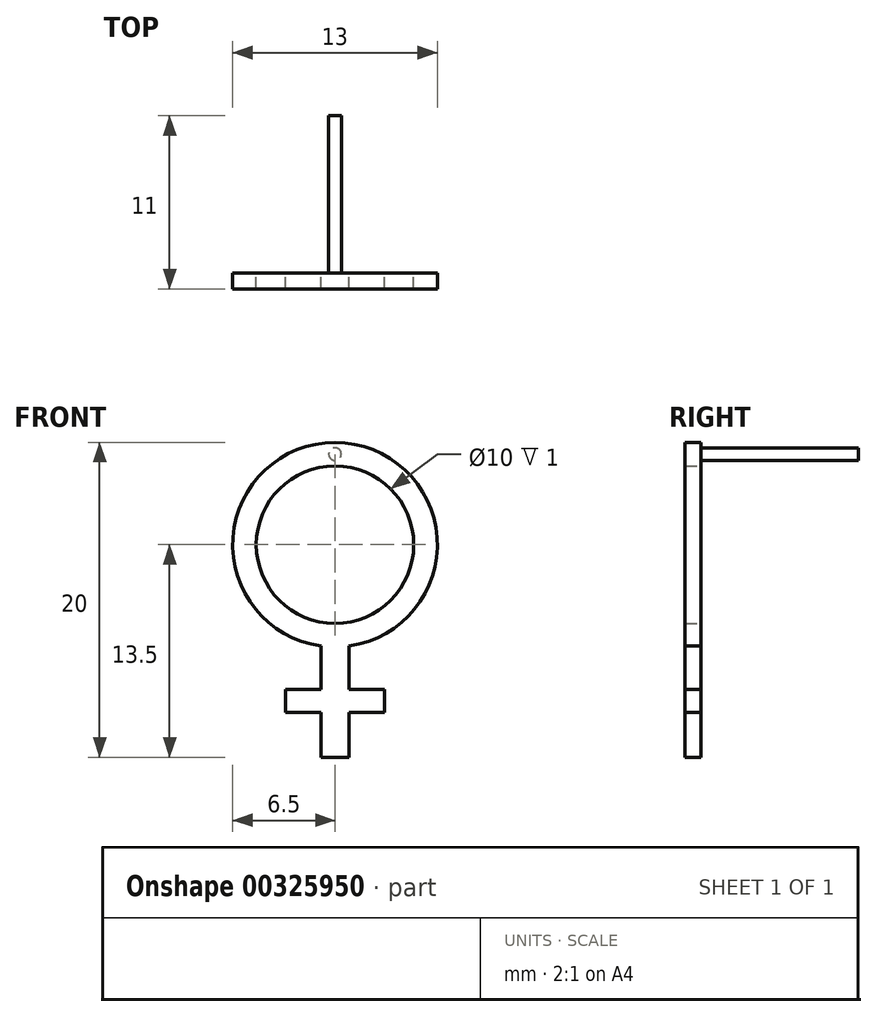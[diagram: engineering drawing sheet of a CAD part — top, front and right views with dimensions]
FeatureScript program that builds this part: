
annotation { "Feature Type Name" : "Feature", "Feature Type Description" : "" }
export const myFeature = defineFeature(function(context is Context, id is Id, definition is map)
    precondition{}
    {
        {
            var Q0;
            Q0=qCreatedBy(makeId("Front.planeOp"),FACE);
            var sketch = newSketch(context, id + "F0", { "sketchPlane" : qUnion([Q0])});
            skCircle(sketch, "E0", {"center": v(0, 0) * mm, "radius": 6.5 * mm});
            skLineSegment(sketch, "E1", {"start": v(0, -6.5) * mm, "end": v(0, -13.5) * mm});
            skCircle(sketch, "E2", {"center": v(0, 0) * mm, "radius": 5 * mm});
            skLineSegment(sketch, "E3", {"start": v(-0.9, -6.44) * mm, "end": v(-0.9, -9.2) * mm});
            skLineSegment(sketch, "E4", {"start": v(-0.9, -9.2) * mm, "end": v(-3.14, -9.2) * mm});
            skLineSegment(sketch, "E5", {"start": v(-3.14, -9.2) * mm, "end": v(-3.14, -10.67) * mm});
            skLineSegment(sketch, "E6", {"start": v(-3.14, -10.67) * mm, "end": v(-0.9, -10.67) * mm});
            skLineSegment(sketch, "E7", {"start": v(-0.9, -10.67) * mm, "end": v(-0.9, -13.5) * mm});
            skLineSegment(sketch, "E8", {"start": v(-0.9, -13.5) * mm, "end": v(0, -13.5) * mm});
            skLineSegment(sketch, "E9.MirrorCS", {"start": v(0.9, -6.44) * mm, "end": v(0.9, -9.2) * mm});
            skLineSegment(sketch, "E10.MirrorCS", {"start": v(0.9, -9.2) * mm, "end": v(3.14, -9.2) * mm});
            skLineSegment(sketch, "E11.MirrorCS", {"start": v(3.14, -9.2) * mm, "end": v(3.14, -10.67) * mm});
            skLineSegment(sketch, "E12.MirrorCS", {"start": v(3.14, -10.67) * mm, "end": v(0.9, -10.67) * mm});
            skLineSegment(sketch, "E13.MirrorCS", {"start": v(0.9, -10.67) * mm, "end": v(0.9, -13.5) * mm});
            skLineSegment(sketch, "E14.MirrorCS", {"start": v(0.9, -13.5) * mm, "end": v(0, -13.5) * mm});
            skSolve(sketch);
        }
        {
            var Q0;
            Q0=makeQuery(id+"F0.imprint","IMPRINT",FACE,{"disambiguationData":[TD([[makeQuery(id+"F0.imprint","IMPRINT",EDGE,{"derivedFrom":sQuery(id+"F0.wireOp",EDGE,"E2")}),-1.0]])]});
            var Q1;
            {var subQ1=sQuery(id+"F0.wireOp",EDGE,"E1");Q1=makeQuery(id+"F0.imprint","IMPRINT",FACE,{"disambiguationData":[TD([[makeQuery(id+"F0.imprint","IMPRINT",EDGE,{"derivedFrom":subQ1}),-1.0]])]});}
            var Q2;
            {var subQ1=sQuery(id+"F0.wireOp",EDGE,"E1");Q2=makeQuery(id+"F0.imprint","IMPRINT",FACE,{"disambiguationData":[TD([[makeQuery(id+"F0.imprint","IMPRINT",EDGE,{"derivedFrom":subQ1}),1.0]])]});}
            extrude(context, id + "F1", {"entities" : qUnion([Q0, Q1, Q2]), "depth" : 1 * mm, "offsetDistance" : 25.4 * mm});
        }
        {
            var Q0;
            Q0=makeQuery(id+"F1.opExtrude","CAP_FACE",FACE,{"disambiguationData":[OSD([sQuery(id+"F0.wireOp",EDGE,"E0"),sQuery(id+"F0.wireOp",EDGE,"E2"),sQuery(id+"F0.wireOp",EDGE,"E3"),sQuery(id+"F0.wireOp",EDGE,"E4"),sQuery(id+"F0.wireOp",EDGE,"E5"),sQuery(id+"F0.wireOp",EDGE,"E6"),sQuery(id+"F0.wireOp",EDGE,"E7"),sQuery(id+"F0.wireOp",EDGE,"E8"),sQuery(id+"F0.wireOp",EDGE,"E9.MirrorCS"),sQuery(id+"F0.wireOp",EDGE,"E10.MirrorCS"),sQuery(id+"F0.wireOp",EDGE,"E11.MirrorCS"),sQuery(id+"F0.wireOp",EDGE,"E12.MirrorCS"),sQuery(id+"F0.wireOp",EDGE,"E13.MirrorCS"),sQuery(id+"F0.wireOp",EDGE,"E14.MirrorCS")])],"isStart":true});
            var sketch = newSketch(context, id + "F2", { "sketchPlane" : qUnion([Q0])});
            skCircle(sketch, "E15", {"center": v(0, 5.75) * mm, "radius": 0.4 * mm});
            skSolve(sketch);
        }
        {
            var Q0;
            Q0=makeQuery(id+"F2.imprint","IMPRINT",FACE,{"disambiguationData":[TD([[makeQuery(id+"F2.imprint","IMPRINT",EDGE,{"derivedFrom":sQuery(id+"F2.wireOp",EDGE,"E15")}),1.0]])]});
            extrude(context, id + "F3", {"entities" : qUnion([Q0]), "operationType" : NewBodyOperationType.ADD, "depth" : 10 * mm, "offsetDistance" : 25.4 * mm});
        }
    });
